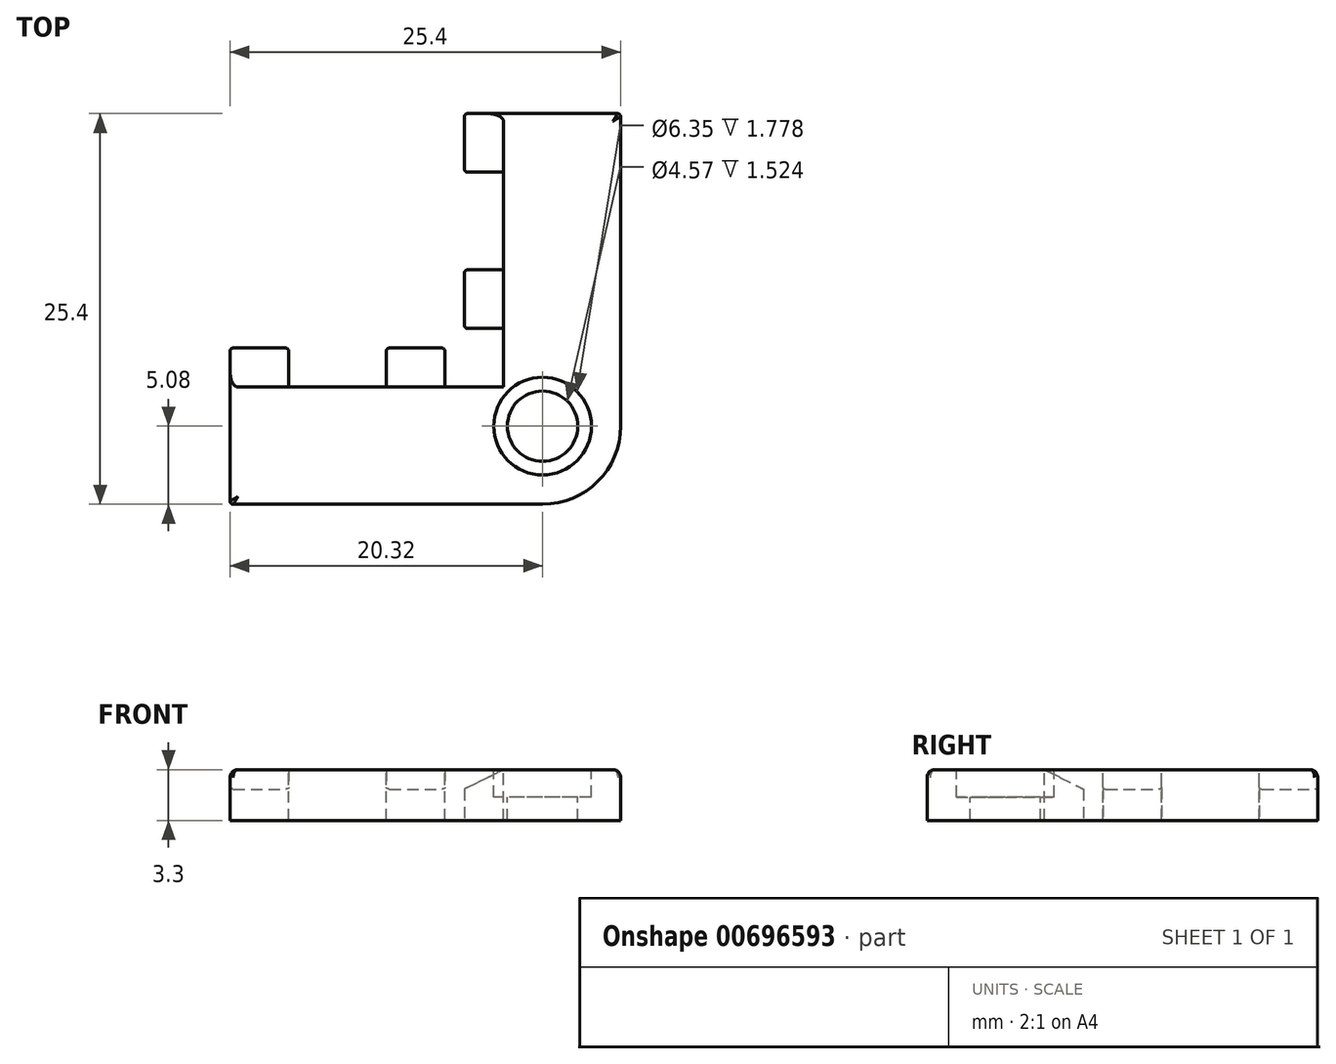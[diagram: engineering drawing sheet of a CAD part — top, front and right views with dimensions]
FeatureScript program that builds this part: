
annotation { "Feature Type Name" : "Feature", "Feature Type Description" : "" }
export const myFeature = defineFeature(function(context is Context, id is Id, definition is map)
    precondition{}
    {
        {
            var Q0;
            Q0=qCreatedBy(makeId("Top.planeOp"),FACE);
            var sketch = newSketch(context, id + "F0", { "sketchPlane" : qUnion([Q0])});
            skLineSegment(sketch, "E0.top", {"start": v(0, 15.24) * mm, "end": v(10.16, 15.24) * mm});
            skLineSegment(sketch, "E0.left", {"start": v(0, 0) * mm, "end": v(0, 15.24) * mm});
            skLineSegment(sketch, "E0.right", {"start": v(10.16, -0.2) * mm, "end": v(10.16, 15.24) * mm});
            skLineSegment(sketch, "E1.bottom", {"start": v(0, 0) * mm, "end": v(-15.24, 0) * mm});
            skLineSegment(sketch, "E1.top", {"start": v(0, -10.16) * mm, "end": v(-15.24, -10.16) * mm});
            skLineSegment(sketch, "E1.right", {"start": v(-15.24, 0) * mm, "end": v(-15.24, -10.16) * mm});
            skLineSegment(sketch, "E2.bottom", {"start": v(-15.24, -10.16) * mm, "end": v(10.16, -10.16) * mm, "construction": true});
            skLineSegment(sketch, "E2.top", {"start": v(-15.24, 15.24) * mm, "end": v(10.16, 15.24) * mm, "construction": true});
            skLineSegment(sketch, "E2.left", {"start": v(-15.24, -10.16) * mm, "end": v(-15.24, 15.24) * mm, "construction": true});
            skLineSegment(sketch, "E2.right", {"start": v(10.16, -10.16) * mm, "end": v(10.16, 15.24) * mm, "construction": true});
            skLineSegment(sketch, "E3.top", {"start": v(0, -10.16) * mm, "end": v(10.16, -10.16) * mm});
            skLineSegment(sketch, "E3.right", {"start": v(10.16, -0.2) * mm, "end": v(10.16, -10.16) * mm});
            skSolve(sketch);
        }
        {
            var Q0;
            Q0 = qSketchRegion(id + "F0", true);
            extrude(context, id + "F1", {"entities" : qUnion([Q0]), "depth" : 3.3 * mm, "offsetDistance" : 25.4 * mm});
        }
        {
            var Q0;
            Q0=makeQuery(id+"F1.opExtrude","CAP_FACE",FACE,{"disambiguationData":[OSD([sQuery(id+"F0.wireOp",EDGE,"E0.top"),sQuery(id+"F0.wireOp",EDGE,"E0.left"),sQuery(id+"F0.wireOp",EDGE,"E0.right"),sQuery(id+"F0.wireOp",EDGE,"E1.bottom"),sQuery(id+"F0.wireOp",EDGE,"E1.top"),sQuery(id+"F0.wireOp",EDGE,"E1.right"),sQuery(id+"F0.wireOp",EDGE,"E3.top"),sQuery(id+"F0.wireOp",EDGE,"E3.right")])],"isStart":false});
            var sketch = newSketch(context, id + "F2", { "sketchPlane" : qUnion([Q0])});
            skLineSegment(sketch, "E4.bottom", {"start": v(10.16, -10.16) * mm, "end": v(5.08, -10.16) * mm, "construction": true});
            skLineSegment(sketch, "E4.top", {"start": v(10.16, -5.08) * mm, "end": v(5.08, -5.08) * mm, "construction": true});
            skLineSegment(sketch, "E4.left", {"start": v(10.16, -10.16) * mm, "end": v(10.16, -5.08) * mm, "construction": true});
            skLineSegment(sketch, "E4.right", {"start": v(5.08, -10.16) * mm, "end": v(5.08, -5.08) * mm, "construction": true});
            skCircle(sketch, "E5", {"center": v(5.08, -5.08) * mm, "radius": 3.18 * mm});
            skSolve(sketch);
        }
        {
            var Q0;
            Q0=makeQuery(id+"F1.opExtrude","SWEPT_EDGE",EDGE,{"disambiguationData":[OSD([sQuery(id+"F0.wireOp",EDGE,"E3.top"),sQuery(id+"F0.wireOp",EDGE,"E3.right")])]});
            fillet(context, id + "F3", {"entities" : qUnion([Q0]), "radius" : 5.08 * mm, "tangentPropagation" : true, "allowEdgeOverflow" : false});
        }
        {
            var Q0;
            Q0 = qSketchRegion(id + "F2", true);
            extrude(context, id + "F4", {"entities" : qUnion([Q0]), "operationType" : NewBodyOperationType.REMOVE, "oppositeDirection" : true, "depth" : 1.78 * mm, "offsetDistance" : 25.4 * mm});
        }
        {
            var Q0;
            Q0=makeQuery(id+"F4.boolean.opBoolean","COPY",FACE,{"derivedFrom":makeQuery(id+"F4.opExtrude","CAP_FACE",FACE,{"disambiguationData":[OSD([sQuery(id+"F2.wireOp",EDGE,"E5")])],"isStart":false})});
            var sketch = newSketch(context, id + "F5", { "sketchPlane" : qUnion([Q0])});
            skCircle(sketch, "E6", {"center": v(5.08, -5.08) * mm, "radius": 2.29 * mm});
            skSolve(sketch);
        }
        {
            var Q0;
            Q0 = qSketchRegion(id + "F5", true);
            extrude(context, id + "F6", {"entities" : qUnion([Q0]), "operationType" : NewBodyOperationType.REMOVE, "oppositeDirection" : true, "depth" : 25.4 * mm, "offsetDistance" : 25.4 * mm});
        }
        {
            var Q0;
            Q0=makeQuery(id+"F1.opExtrude","CAP_EDGE",EDGE,{"disambiguationData":[OSD([sQuery(id+"F0.wireOp",EDGE,"E1.bottom")])],"isStart":false});
            var Q1;
            Q1=makeQuery(id+"F1.opExtrude","CAP_EDGE",EDGE,{"disambiguationData":[OSD([sQuery(id+"F0.wireOp",EDGE,"E0.left")])],"isStart":false});
            chamfer(context, id + "F7", {"entities" : qUnion([Q0, Q1]), "chamferType" : ChamferType.TWO_OFFSETS, "width1" : 2.54 * mm, "oppositeDirection" : false, "width2" : 1.27 * mm, "tangentPropagation" : true});
        }
        {
            var Q0;
            Q0=makeQuery(id+"F1.opExtrude","CAP_FACE",FACE,{"disambiguationData":[OSD([sQuery(id+"F0.wireOp",EDGE,"E0.top"),sQuery(id+"F0.wireOp",EDGE,"E0.left"),sQuery(id+"F0.wireOp",EDGE,"E0.right"),sQuery(id+"F0.wireOp",EDGE,"E1.bottom"),sQuery(id+"F0.wireOp",EDGE,"E1.top"),sQuery(id+"F0.wireOp",EDGE,"E1.right"),sQuery(id+"F0.wireOp",EDGE,"E3.top"),sQuery(id+"F0.wireOp",EDGE,"E3.right")])],"isStart":false});
            var sketch = newSketch(context, id + "F8", { "sketchPlane" : qUnion([Q0])});
            skLineSegment(sketch, "E7.bottom", {"start": v(2.54, -2.54) * mm, "end": v(-1.27, -2.54) * mm});
            skLineSegment(sketch, "E7.top", {"start": v(2.54, 1.27) * mm, "end": v(-1.27, 1.27) * mm});
            skLineSegment(sketch, "E7.left", {"start": v(2.54, -2.54) * mm, "end": v(2.54, 1.27) * mm});
            skLineSegment(sketch, "E7.right", {"start": v(-1.27, -2.54) * mm, "end": v(-1.27, 1.27) * mm});
            skLineSegment(sketch, "E8.bottom", {"start": v(2.54, 5.08) * mm, "end": v(-1.27, 5.08) * mm});
            skLineSegment(sketch, "E8.top", {"start": v(2.54, 11.43) * mm, "end": v(-1.27, 11.43) * mm});
            skLineSegment(sketch, "E8.left", {"start": v(2.54, 5.08) * mm, "end": v(2.54, 11.43) * mm});
            skLineSegment(sketch, "E8.right", {"start": v(-1.27, 5.08) * mm, "end": v(-1.27, 11.43) * mm});
            skLineSegment(sketch, "E9.bottom", {"start": v(-5.08, -2.54) * mm, "end": v(-11.43, -2.54) * mm});
            skLineSegment(sketch, "E9.top", {"start": v(-5.08, 1.27) * mm, "end": v(-11.43, 1.27) * mm});
            skLineSegment(sketch, "E9.left", {"start": v(-5.08, -2.54) * mm, "end": v(-5.08, 1.27) * mm});
            skLineSegment(sketch, "E9.right", {"start": v(-11.43, -2.54) * mm, "end": v(-11.43, 1.27) * mm});
            skSolve(sketch);
        }
        {
            var Q0;
            Q0 = qSketchRegion(id + "F8", true);
            extrude(context, id + "F9", {"entities" : qUnion([Q0]), "operationType" : NewBodyOperationType.REMOVE, "oppositeDirection" : true, "depth" : 25.4 * mm, "offsetDistance" : 25.4 * mm});
        }
        {
            var Q0;
            Q0=makeQuery(id+"F1.opExtrude","SWEPT_EDGE",EDGE,{"disambiguationData":[OSD([sQuery(id+"F0.wireOp",EDGE,"E0.top"),sQuery(id+"F0.wireOp",EDGE,"E0.left")])]});
            var Q1;
            Q1=makeQuery(id+"F9.boolean.opBoolean","INTERSECT",EDGE,{"derivedFrom":[makeQuery(id+"F1.opExtrude","SWEPT_FACE",FACE,{"disambiguationData":[OSD([sQuery(id+"F0.wireOp",EDGE,"E0.left")])]}),makeQuery(id+"F9.opExtrude","SWEPT_FACE",FACE,{"disambiguationData":[OSD([sQuery(id+"F8.wireOp",EDGE,"E8.top")])]})]});
            var Q2;
            Q2=makeQuery(id+"F9.boolean.opBoolean","INTERSECT",EDGE,{"derivedFrom":[makeQuery(id+"F1.opExtrude","SWEPT_FACE",FACE,{"disambiguationData":[OSD([sQuery(id+"F0.wireOp",EDGE,"E0.left")])]}),makeQuery(id+"F9.opExtrude","SWEPT_FACE",FACE,{"disambiguationData":[OSD([sQuery(id+"F8.wireOp",EDGE,"E8.bottom")])]})]});
            var Q3;
            Q3=makeQuery(id+"F9.boolean.opBoolean","INTERSECT",EDGE,{"derivedFrom":[makeQuery(id+"F1.opExtrude","SWEPT_FACE",FACE,{"disambiguationData":[OSD([sQuery(id+"F0.wireOp",EDGE,"E0.left")])]}),makeQuery(id+"F9.opExtrude","SWEPT_FACE",FACE,{"disambiguationData":[OSD([sQuery(id+"F8.wireOp",EDGE,"E7.top")])]})]});
            var Q4;
            Q4=makeQuery(id+"F9.boolean.opBoolean","INTERSECT",EDGE,{"derivedFrom":[makeQuery(id+"F1.opExtrude","SWEPT_FACE",FACE,{"disambiguationData":[OSD([sQuery(id+"F0.wireOp",EDGE,"E1.bottom")])]}),makeQuery(id+"F9.opExtrude","SWEPT_FACE",FACE,{"disambiguationData":[OSD([sQuery(id+"F8.wireOp",EDGE,"E7.right")])]})]});
            var Q5;
            Q5=makeQuery(id+"F9.boolean.opBoolean","INTERSECT",EDGE,{"derivedFrom":[makeQuery(id+"F1.opExtrude","SWEPT_FACE",FACE,{"disambiguationData":[OSD([sQuery(id+"F0.wireOp",EDGE,"E1.bottom")])]}),makeQuery(id+"F9.opExtrude","SWEPT_FACE",FACE,{"disambiguationData":[OSD([sQuery(id+"F8.wireOp",EDGE,"E9.left")])]})]});
            var Q6;
            Q6=makeQuery(id+"F9.boolean.opBoolean","INTERSECT",EDGE,{"derivedFrom":[makeQuery(id+"F1.opExtrude","SWEPT_FACE",FACE,{"disambiguationData":[OSD([sQuery(id+"F0.wireOp",EDGE,"E1.bottom")])]}),makeQuery(id+"F9.opExtrude","SWEPT_FACE",FACE,{"disambiguationData":[OSD([sQuery(id+"F8.wireOp",EDGE,"E9.right")])]})]});
            var Q7;
            Q7=makeQuery(id+"F1.opExtrude","SWEPT_EDGE",EDGE,{"disambiguationData":[OSD([sQuery(id+"F0.wireOp",EDGE,"E1.bottom"),sQuery(id+"F0.wireOp",EDGE,"E1.right")])]});
            var Q8;
            Q8=makeQuery(id+"F1.opExtrude","SWEPT_EDGE",EDGE,{"disambiguationData":[OSD([sQuery(id+"F0.wireOp",EDGE,"E1.top"),sQuery(id+"F0.wireOp",EDGE,"E1.right")])]});
            var Q9;
            Q9=makeQuery(id+"F1.opExtrude","SWEPT_EDGE",EDGE,{"disambiguationData":[OSD([sQuery(id+"F0.wireOp",EDGE,"E0.top"),sQuery(id+"F0.wireOp",EDGE,"E0.right")])]});
            fillet(context, id + "F10", {"entities" : qUnion([Q0, Q1, Q2, Q3, Q4, Q5, Q6, Q7, Q8, Q9]), "radius" : .2 * mm, "tangentPropagation" : true, "allowEdgeOverflow" : false});
        }
        {
            var Q0;
            Q0=makeQuery(id+"F1.opExtrude","CAP_EDGE",EDGE,{"disambiguationData":[OSD([sQuery(id+"F0.wireOp",EDGE,"E1.top"),sQuery(id+"F0.wireOp",EDGE,"E3.top")])],"isStart":false});
            fillet(context, id + "F11", {"entities" : qUnion([Q0]), "radius" : 0.5 * mm, "tangentPropagation" : true, "allowEdgeOverflow" : false});
        }
    });
